# Revit family: Bath-Alcove_Heated_Surface-KOHLER-Mariposa-K-1242
name_source: partatom
category: Plumbing Fixtures
units: mm (PartAtom-declared; Revit-internal decimal feet)

## family parameters
Cut with Voids When Loaded = No
Host = Face
OmniClass Number = 23.31.15.00
OmniClass Title = Bathtubs
Part Type = Normal
Room Calculation Point = No
Round Connector Dimension = Use Diameter
Shared = No

## types (6) — shared parameters
ADA Compliant = No
Assembly Code = D2010500
CW Connection = No
Cold Water Inlet = Cold Water Inlet
Date Modified = 09/26/2023
Default Elevation = 0"
Drain Included = No
HW Connection = No
Height = 21 5/16"
Hot Water Inlet = Hot Water Inlet
Length = 60 1/8"
Manufacturer = Kohler Co.
Master Format 2014 = 22 41 19
Master Format 2014 Name = Residential Bathtubs
Material = Acrylic
Product Documentation Link = https://www.us.kohler.com
Product Name = Mariposa
Product Page URL = http://www.us.kohler.com
URL = https://www.us.kohler.com
Vent Connection = No
Waste Connection = Yes
Waste Water Outlet = Waste Water Outlet
WaterSense Certified = No
Width = 36 1/16"

## per-type parameters (varying)
| type | Description | Distance | Finish | Left Drain | Model | Right Drain | Type |
| Left Drain, 0-White | 60 Inch x 36 Inch alcove bath with Bask heated surface, left drain | 51 3/8" | KOHLER-Acrylic-0-White | Yes | K-1242-LW-0 | No | 1 |
| Left Drain, 96-Biscuit | 60 Inch x 36 Inch alcove bath with Bask heated surface, left drain | 51 3/8" | KOHLER-Acrylic-96-Biscuit | Yes | K-1242-LW-96 | No | 2 |
| Left Drain, NY-Dune | 60 Inch x 36 Inch alcove bath with Bask heated surface, left drain | 51 3/8" | KOHLER-Acrylic-NY-Dune | Yes | K-1242-LW-NY | No | 3 |
| Right Drain, 0-White | 60 Inch x 36 Inch alcove bath with Bask heated surface, right drain | 8 3/4" | KOHLER-Acrylic-0-White | No | K-1242-RW-0 | Yes | 4 |
| Right Drain, 96-Biscuit | 60 Inch x 36 Inch alcove bath with Bask heated surface, right drain | 8 3/4" | KOHLER-Acrylic-96-Biscuit | No | K-1242-RW-96 | Yes | 5 |
| Right Drain, NY-Dune | 60 Inch x 36 Inch alcove bath with Bask heated surface, right drain | 8 3/4" | KOHLER-Acrylic-NY-Dune | No | K-1242-RW-NY | Yes | 6 |

## geometry (parser evidence)
native form markers: Sweep x5
no freeform markers — native parametric forms only
